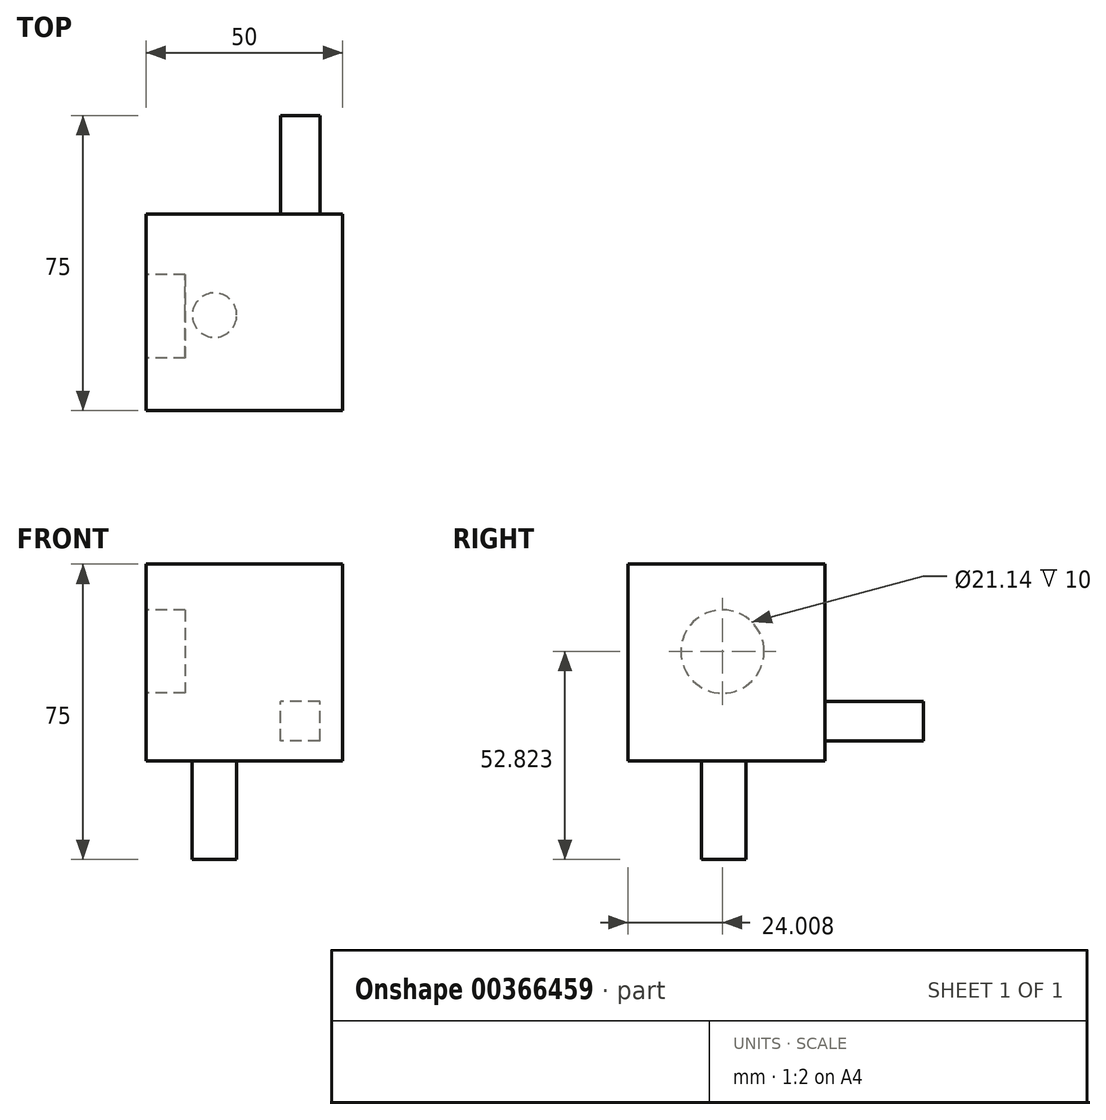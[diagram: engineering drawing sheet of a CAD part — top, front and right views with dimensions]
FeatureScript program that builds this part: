
annotation { "Feature Type Name" : "Feature", "Feature Type Description" : "" }
export const myFeature = defineFeature(function(context is Context, id is Id, definition is map)
    precondition{}
    {
        {
            var Q0;
            Q0=qCreatedBy(makeId("Front.planeOp"),FACE);
            var sketch = newSketch(context, id + "F0", { "sketchPlane" : qUnion([Q0])});
            skLineSegment(sketch, "E0.bottom", {"start": v(0, 0) * mm, "end": v(-50, 0) * mm});
            skLineSegment(sketch, "E0.top", {"start": v(0, 50) * mm, "end": v(-50, 50) * mm});
            skLineSegment(sketch, "E0.left", {"start": v(0, 0) * mm, "end": v(0, 50) * mm});
            skLineSegment(sketch, "E0.right", {"start": v(-50, 0) * mm, "end": v(-50, 50) * mm});
            skSolve(sketch);
        }
        {
            var Q0;
            Q0=makeQuery(id+"F0.imprint","IMPRINT",FACE,{"disambiguationData":[TD([[makeQuery(id+"F0.imprint","IMPRINT",EDGE,{"derivedFrom":sQuery(id+"F0.wireOp",EDGE,"E0.bottom")}),-1.0]])]});
            extrude(context, id + "F1", {"entities" : qUnion([Q0]), "depth" : 50 * mm});
        }
        {
            var Q0;
            Q0=makeQuery(id+"F1.opExtrude","SWEPT_FACE",FACE,{"disambiguationData":[OSD([sQuery(id+"F0.wireOp",EDGE,"E0.bottom")])]});
            var sketch = newSketch(context, id + "F2", { "sketchPlane" : qUnion([Q0])});
            skCircle(sketch, "E1", {"center": v(-32.57, 25.7) * mm, "radius": 5.65 * mm});
            skSolve(sketch);
        }
        {
            var Q0;
            Q0=makeQuery(id+"F2.imprint","IMPRINT",FACE,{"disambiguationData":[TD([[makeQuery(id+"F2.imprint","IMPRINT",EDGE,{"derivedFrom":sQuery(id+"F2.wireOp",EDGE,"E1")}),1.0]])]});
            extrude(context, id + "F3", {"entities" : qUnion([Q0]), "operationType" : NewBodyOperationType.ADD, "depth" : 25 * mm});
        }
        {
            var Q0;
            Q0=makeQuery(id+"F1.opExtrude","SWEPT_FACE",FACE,{"disambiguationData":[OSD([sQuery(id+"F0.wireOp",EDGE,"E0.right")])]});
            var sketch = newSketch(context, id + "F4", { "sketchPlane" : qUnion([Q0])});
            skCircle(sketch, "E2", {"center": v(26, 27.82) * mm, "radius": 10.57 * mm});
            skSolve(sketch);
        }
        {
            var Q0;
            Q0=makeQuery(id+"F4.imprint","IMPRINT",FACE,{"disambiguationData":[TD([[makeQuery(id+"F4.imprint","IMPRINT",EDGE,{"derivedFrom":sQuery(id+"F4.wireOp",EDGE,"E2")}),1.0]])]});
            extrude(context, id + "F5", {"entities" : qUnion([Q0]), "operationType" : NewBodyOperationType.REMOVE, "oppositeDirection" : true, "depth" : 10 * mm});
        }
        {
            var Q0;
            Q0=makeQuery(id+"F1.opExtrude","CAP_FACE",FACE,{"disambiguationData":[OSD([sQuery(id+"F0.wireOp",EDGE,"E0.bottom"),sQuery(id+"F0.wireOp",EDGE,"E0.top"),sQuery(id+"F0.wireOp",EDGE,"E0.left"),sQuery(id+"F0.wireOp",EDGE,"E0.right")])],"isStart":true});
            var sketch = newSketch(context, id + "F6", { "sketchPlane" : qUnion([Q0])});
            skLineSegment(sketch, "E3.bottom", {"start": v(5.81, 5.13) * mm, "end": v(15.81, 5.13) * mm});
            skLineSegment(sketch, "E3.top", {"start": v(5.81, 15.13) * mm, "end": v(15.81, 15.13) * mm});
            skLineSegment(sketch, "E3.left", {"start": v(5.81, 5.13) * mm, "end": v(5.81, 15.13) * mm});
            skLineSegment(sketch, "E3.right", {"start": v(15.81, 5.13) * mm, "end": v(15.81, 15.13) * mm});
            skLineSegment(sketch, "E4.bottom", {"start": v(30, 5.13) * mm, "end": v(40, 5.13) * mm});
            skLineSegment(sketch, "E4.top", {"start": v(30, 15.13) * mm, "end": v(40, 15.13) * mm});
            skLineSegment(sketch, "E4.left", {"start": v(30, 5.13) * mm, "end": v(30, 15.13) * mm});
            skLineSegment(sketch, "E4.right", {"start": v(40, 5.13) * mm, "end": v(40, 15.13) * mm});
            skSolve(sketch);
        }
        {
            var Q0;
            Q0=makeQuery(id+"F6.imprint","IMPRINT",FACE,{"disambiguationData":[TD([[makeQuery(id+"F6.imprint","IMPRINT",EDGE,{"derivedFrom":sQuery(id+"F6.wireOp",EDGE,"E3.bottom")}),1.0]])]});
            extrude(context, id + "F7", {"entities" : qUnion([Q0]), "operationType" : NewBodyOperationType.ADD, "depth" : 25 * mm});
        }
    });
